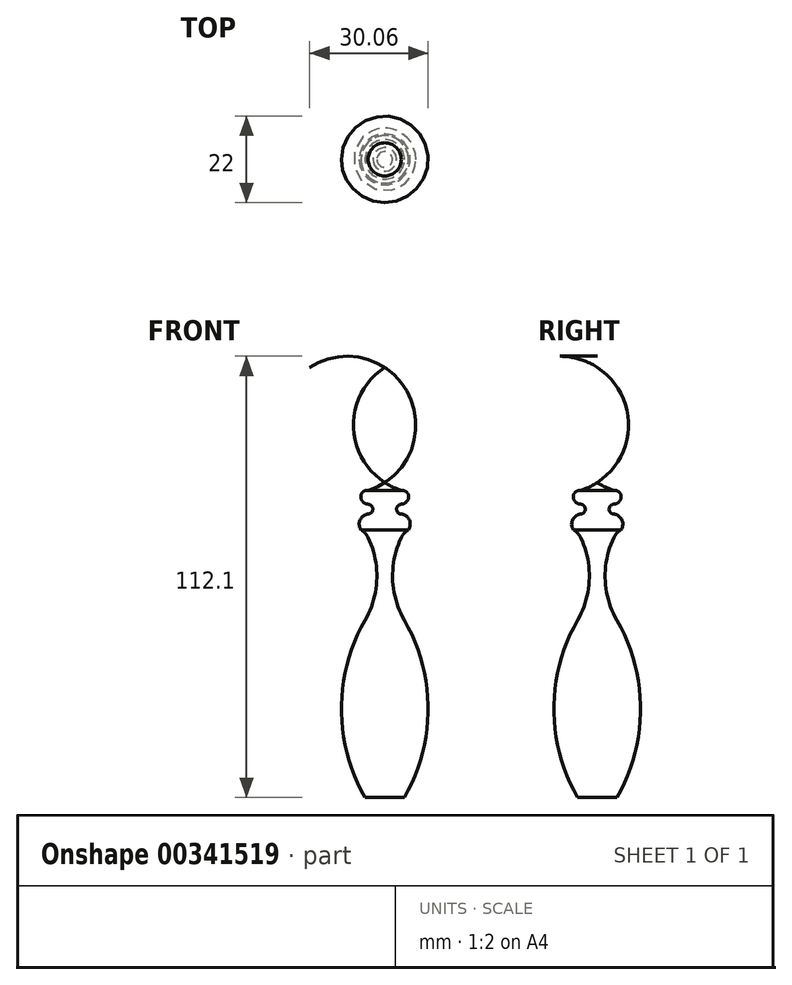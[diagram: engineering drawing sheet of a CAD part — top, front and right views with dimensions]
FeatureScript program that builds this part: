
annotation { "Feature Type Name" : "Feature", "Feature Type Description" : "" }
export const myFeature = defineFeature(function(context is Context, id is Id, definition is map)
    precondition{}
    {
        {
            var Q0;
            Q0=qCreatedBy(makeId("Front.planeOp"),FACE);
            var sketch = newSketch(context, id + "F0", { "sketchPlane" : qUnion([Q0])});
            skLineSegment(sketch, "E0", {"start": v(5, -80) * mm, "end": v(0, -80) * mm});
            skLineSegment(sketch, "E1", {"start": v(0, -80) * mm, "end": v(0, 0) * mm});
            skArc(sketch, "E2", {"start": v(5, -80) * mm, "mid": v(11, -57.5) * mm, "end": v(5, -35) * mm});
            skArc(sketch, "E3", {"start": v(4.21, -14) * mm, "mid": v(2.02, -24.6) * mm, "end": v(5, -35) * mm});
            skArc(sketch, "E4", {"start": v(4.21, -5.5) * mm, "mid": v(5.4, -5.03) * mm, "end": v(6.05, -3.92) * mm});
            skArc(sketch, "E5", {"start": v(4.21, -5.5) * mm, "mid": v(3.02, -6.72) * mm, "end": v(4.16, -8) * mm});
            skArc(sketch, "E6", {"start": v(6.05, -12) * mm, "mid": v(6.24, -9.46) * mm, "end": v(4.16, -8) * mm});
            skArc(sketch, "E7", {"start": v(6.05, -12) * mm, "mid": v(4.98, -12.86) * mm, "end": v(4.21, -14) * mm});
            skArc(sketch, "E8", {"start": v(6.05, -3.92) * mm, "mid": v(5.63, -2.48) * mm, "end": v(4.21, -2) * mm});
            skArc(sketch, "E9", {"start": v(0, 0) * mm, "mid": v(2.04, -1.14) * mm, "end": v(4.21, -2) * mm});
            skSolve(sketch);
        }
        {
            var Q0;
            Q0=makeQuery(id+"F0.imprint","IMPRINT",FACE,{"disambiguationData":[TD([[makeQuery(id+"F0.imprint","IMPRINT",EDGE,{"derivedFrom":sQuery(id+"F0.wireOp",EDGE,"E0")}),-1.0]])]});
            var Q1;
            Q1=sQuery(id+"F0.wireOp",EDGE,"E1");
            revolve(context, id + "F1", {"entities" : qUnion([Q0]), "axis" : qUnion([Q1]), "revolveType" : RevolveType.FULL});
        }
    });
